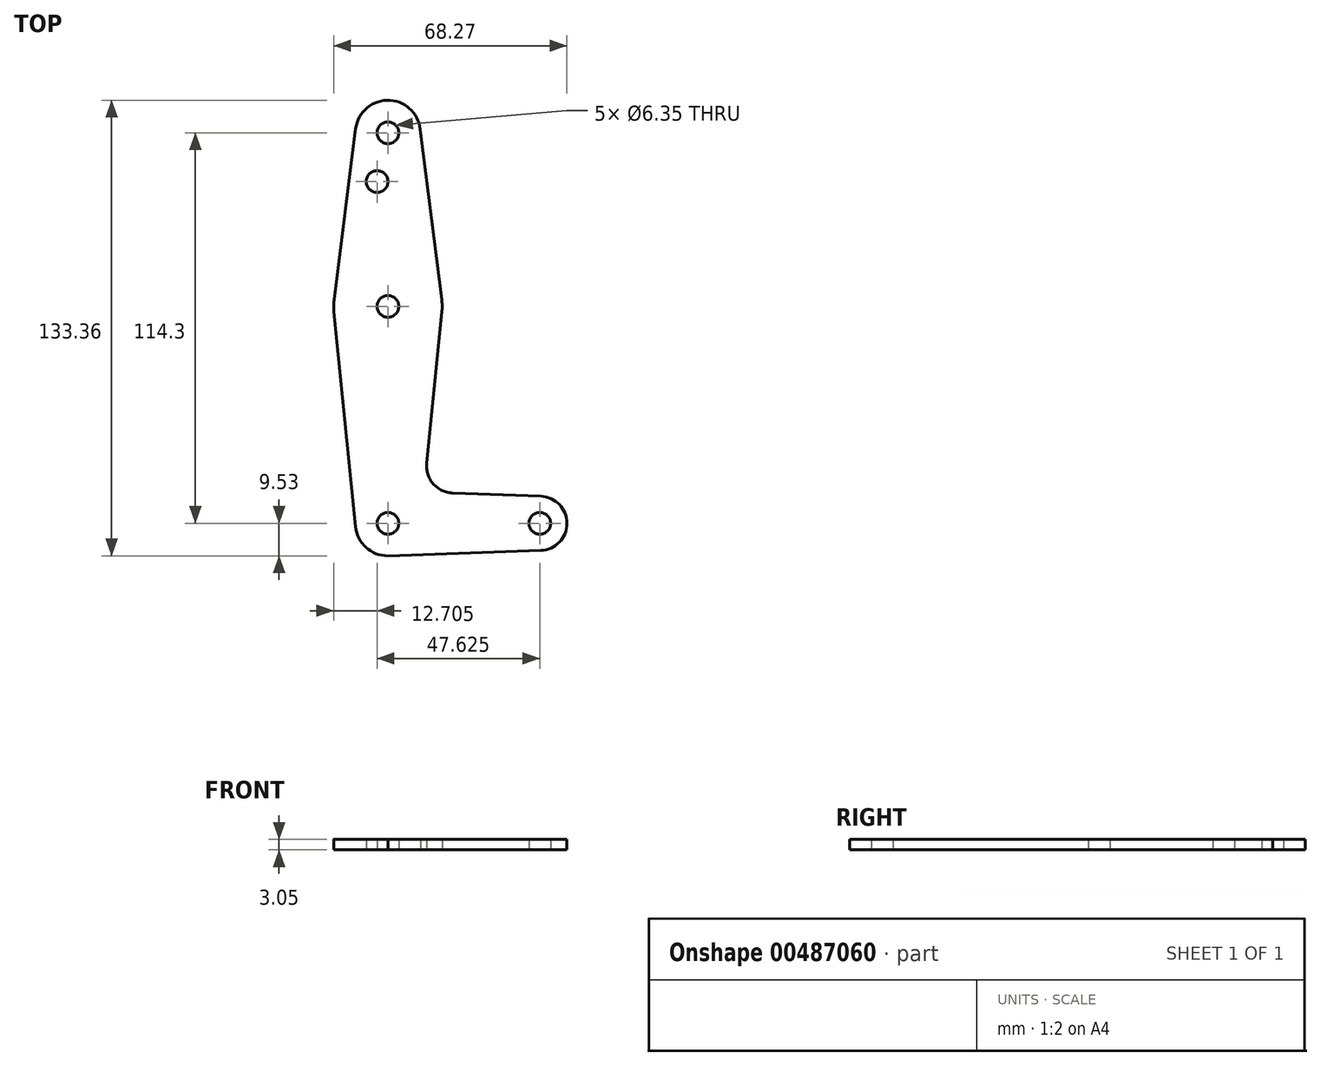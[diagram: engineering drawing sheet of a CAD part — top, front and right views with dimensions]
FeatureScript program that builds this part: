
annotation { "Feature Type Name" : "Feature", "Feature Type Description" : "" }
export const myFeature = defineFeature(function(context is Context, id is Id, definition is map)
    precondition{}
    {
        {
            var Q0;
            Q0=qCreatedBy(makeId("Top.planeOp"),FACE);
            var sketch = newSketch(context, id + "F0", { "sketchPlane" : qUnion([Q0])});
            skLineSegment(sketch, "E0", {"start": v(0, 0) * mm, "end": v(0, 114.3) * mm, "construction": true});
            skLineSegment(sketch, "E1", {"start": v(0, 0) * mm, "end": v(44.45, 0) * mm, "construction": true});
            skCircle(sketch, "E2", {"center": v(0, 0) * mm, "radius": 9.53 * mm});
            skCircle(sketch, "E3", {"center": v(0, 114.3) * mm, "radius": 9.53 * mm});
            skCircle(sketch, "E4", {"center": v(44.45, 0) * mm, "radius": 7.94 * mm});
            skCircle(sketch, "E5", {"center": v(0, 63.5) * mm, "radius": 15.88 * mm});
            skLineSegment(sketch, "E6", {"start": v(9.52, 114.3) * mm, "end": v(15.75, 65.5) * mm});
            skLineSegment(sketch, "E7", {"start": v(-9.45, 115.5) * mm, "end": v(-15.75, 65.48) * mm});
            skLineSegment(sketch, "E8", {"start": v(-15.8, 61.91) * mm, "end": v(-9.48, -0.95) * mm});
            skLineSegment(sketch, "E9", {"start": v(15.8, 61.91) * mm, "end": v(11.34, 17.59) * mm});
            skLineSegment(sketch, "E10", {"start": v(18.97, 8.85) * mm, "end": v(44.73, 7.93) * mm});
            skLineSegment(sketch, "E11", {"start": v(0, -9.52) * mm, "end": v(44.73, -7.93) * mm});
            skCircle(sketch, "E12", {"center": v(0, 114.3) * mm, "radius": 3.18 * mm});
            skCircle(sketch, "E13", {"center": v(0, 63.5) * mm, "radius": 3.18 * mm});
            skCircle(sketch, "E14", {"center": v(0, 0) * mm, "radius": 3.18 * mm});
            skCircle(sketch, "E15", {"center": v(44.45, 0) * mm, "radius": 3.18 * mm});
            skCircle(sketch, "E16", {"center": v(-3.18, 100.03) * mm, "radius": 3.18 * mm});
            skArc(sketch, "E17.filletArc", {"start": v(11.34, 17.59) * mm, "mid": v(13.26, 11.57) * mm, "end": v(18.97, 8.85) * mm});
            skSolve(sketch);
        }
        {
            var Q0;
            Q0=makeQuery(id+"F0.imprint","IMPRINT",FACE,{"disambiguationData":[TD([[makeQuery(id+"F0.imprint","IMPRINT",EDGE,{"derivedFrom":sQuery(id+"F0.wireOp",EDGE,"E12")}),-1.0]])]});
            var Q1;
            {var subQ0=sQuery(id+"F0.wireOp",EDGE,"E6");Q1=makeQuery(id+"F0.imprint","IMPRINT",FACE,{"disambiguationData":[TD([[makeQuery(id+"F0.imprint","IMPRINT",EDGE,{"derivedFrom":subQ0}),-1.0]])]});}
            var Q2;
            Q2=makeQuery(id+"F0.imprint","IMPRINT",FACE,{"disambiguationData":[TD([[makeQuery(id+"F0.imprint","IMPRINT",EDGE,{"derivedFrom":sQuery(id+"F0.wireOp",EDGE,"E13")}),-1.0]])]});
            var Q3;
            {var subQ0=sQuery(id+"F0.wireOp",EDGE,"E8");Q3=makeQuery(id+"F0.imprint","IMPRINT",FACE,{"disambiguationData":[TD([[makeQuery(id+"F0.imprint","IMPRINT",EDGE,{"derivedFrom":subQ0}),1.0]])]});}
            var Q4;
            Q4=makeQuery(id+"F0.imprint","IMPRINT",FACE,{"disambiguationData":[TD([[makeQuery(id+"F0.imprint","IMPRINT",EDGE,{"derivedFrom":sQuery(id+"F0.wireOp",EDGE,"E14")}),-1.0]])]});
            var Q5;
            Q5=makeQuery(id+"F0.imprint","IMPRINT",FACE,{"disambiguationData":[TD([[makeQuery(id+"F0.imprint","IMPRINT",EDGE,{"derivedFrom":sQuery(id+"F0.wireOp",EDGE,"E15")}),-1.0]])]});
            extrude(context, id + "F1", {"entities" : qUnion([Q0, Q1, Q2, Q3, Q4, Q5]), "depth" : 3.05 * mm});
        }
    });
